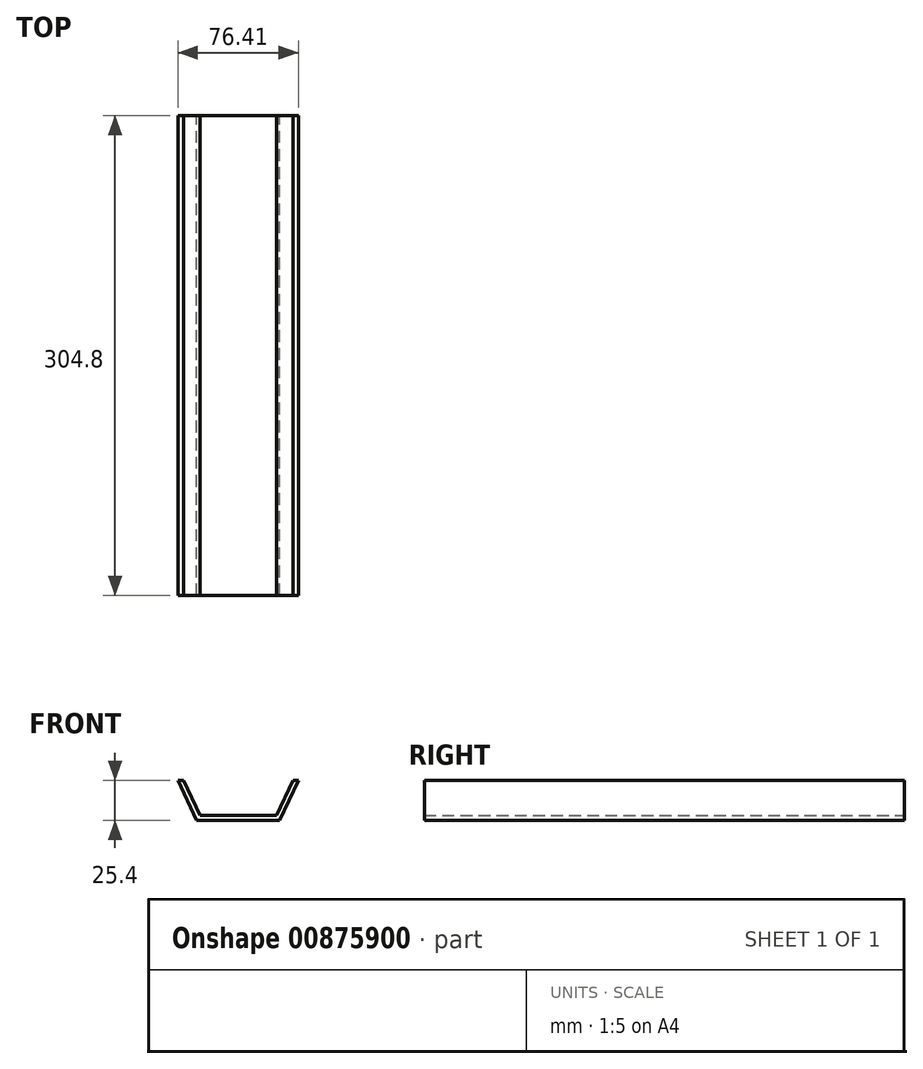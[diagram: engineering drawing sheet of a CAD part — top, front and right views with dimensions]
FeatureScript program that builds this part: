
annotation { "Feature Type Name" : "Feature", "Feature Type Description" : "" }
export const myFeature = defineFeature(function(context is Context, id is Id, definition is map)
    precondition{}
    {
        {
            var Q0;
            Q0=qCreatedBy(makeId("Front.planeOp"),FACE);
            var sketch = newSketch(context, id + "F0", { "sketchPlane" : qUnion([Q0])});
            skLineSegment(sketch, "E0", {"start": v(-27.38, -12.63) * mm, "end": v(25.35, -12.63) * mm});
            skLineSegment(sketch, "E1", {"start": v(-27.38, -12.63) * mm, "end": v(-39.22, 12.77) * mm});
            skPoint(sketch, "E2", {"position": v(-39.22, 12.77) * mm});
            skLineSegment(sketch, "E3", {"start": v(25.35, -12.63) * mm, "end": v(37.2, 12.77) * mm});
            skPoint(sketch, "E4", {"position": v(-27.38, -12.63) * mm});
            skPoint(sketch, "E5", {"position": v(25.35, -12.63) * mm});
            skLineSegment(sketch, "E6", {"start": v(23.33, -9.45) * mm, "end": v(33.69, 12.77) * mm});
            skLineSegment(sketch, "E7", {"start": v(-35.72, 12.77) * mm, "end": v(-25.36, -9.45) * mm});
            skLineSegment(sketch, "E8", {"start": v(-25.36, -9.45) * mm, "end": v(23.33, -9.45) * mm});
            skLineSegment(sketch, "E9", {"start": v(-39.22, 12.77) * mm, "end": v(-35.72, 12.77) * mm});
            skPoint(sketch, "E10", {"position": v(-35.72, 12.77) * mm});
            skLineSegment(sketch, "E11", {"start": v(-35.72, 12.77) * mm, "end": v(33.69, 12.77) * mm, "construction": true});
            skPoint(sketch, "E12", {"position": v(-25.36, -9.45) * mm});
            skPoint(sketch, "E13", {"position": v(23.33, -9.45) * mm});
            skPoint(sketch, "E14", {"position": v(33.69, 12.77) * mm});
            skPoint(sketch, "E15", {"position": v(37.2, 12.77) * mm});
            skLineSegment(sketch, "E16", {"start": v(33.69, 12.77) * mm, "end": v(37.2, 12.77) * mm});
            skSolve(sketch);
        }
        {
            var Q0;
            Q0=makeQuery(id+"F0.imprint","IMPRINT",FACE,{"disambiguationData":[TD([[makeQuery(id+"F0.imprint","IMPRINT",EDGE,{"derivedFrom":sQuery(id+"F0.wireOp",EDGE,"E0")}),1.0]])]});
            extrude(context, id + "F1", {"entities" : qUnion([Q0]), "depth" : 304.8 * mm, "offsetDistance" : 25.4 * mm});
        }
    });
